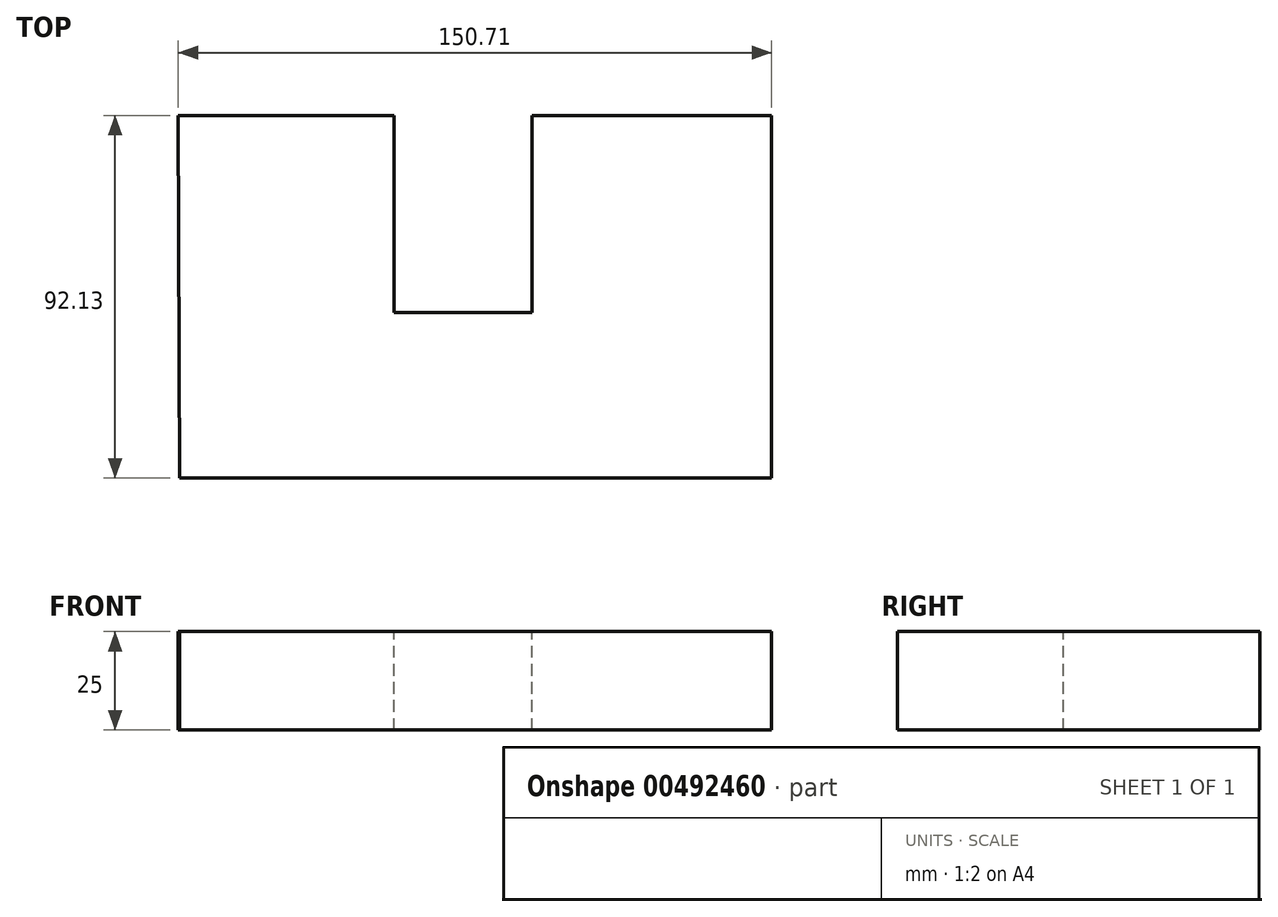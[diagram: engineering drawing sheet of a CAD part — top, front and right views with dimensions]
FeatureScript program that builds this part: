
annotation { "Feature Type Name" : "Feature", "Feature Type Description" : "" }
export const myFeature = defineFeature(function(context is Context, id is Id, definition is map)
    precondition{}
    {
        {
            var Q0;
            Q0=qCreatedBy(makeId("Top.planeOp"),FACE);
            var sketch = newSketch(context, id + "F0", { "sketchPlane" : qUnion([Q0])});
            skLineSegment(sketch, "E0", {"start": v(-75.26, 36.66) * mm, "end": v(75.45, 36.66) * mm});
            skLineSegment(sketch, "E1", {"start": v(75.45, 36.66) * mm, "end": v(75.45, -55.47) * mm});
            skLineSegment(sketch, "E2", {"start": v(-74.87, -55.47) * mm, "end": v(-75.26, 36.66) * mm});
            skLineSegment(sketch, "E3", {"start": v(-74.87, -55.47) * mm, "end": v(75.45, -55.47) * mm});
            skSolve(sketch);
        }
        {
            var Q0;
            Q0=makeQuery(id+"F0.imprint","IMPRINT",FACE,{"disambiguationData":[TD([[makeQuery(id+"F0.imprint","IMPRINT",EDGE,{"derivedFrom":sQuery(id+"F0.wireOp",EDGE,"E0")}),-1.0]])]});
            extrude(context, id + "F1", {"entities" : qUnion([Q0]), "depth" : 25 * mm});
        }
        {
            var Q0;
            Q0=makeQuery(id+"F1.opExtrude","CAP_FACE",FACE,{"disambiguationData":[OSD([sQuery(id+"F0.wireOp",EDGE,"E0"),sQuery(id+"F0.wireOp",EDGE,"E1"),sQuery(id+"F0.wireOp",EDGE,"E2"),sQuery(id+"F0.wireOp",EDGE,"E3")])],"isStart":false});
            var sketch = newSketch(context, id + "F2", { "sketchPlane" : qUnion([Q0])});
            skLineSegment(sketch, "E4", {"start": v(-20.42, 36.66) * mm, "end": v(-20.42, -13.34) * mm});
            skLineSegment(sketch, "E5", {"start": v(14.6, 36.66) * mm, "end": v(14.6, -13.34) * mm});
            skLineSegment(sketch, "E6", {"start": v(-20.42, -13.34) * mm, "end": v(14.6, -13.34) * mm});
            skSolve(sketch);
        }
        {
            var Q0;
            {var subQ0=sQuery(id+"F2.wireOp",EDGE,"E4");Q0=makeQuery(id+"F2.imprint","IMPRINT",FACE,{"disambiguationData":[TD([[makeQuery(id+"F2.imprint","IMPRINT",EDGE,{"derivedFrom":subQ0}),1.0]])]});}
            extrude(context, id + "F3", {"entities" : qUnion([Q0]), "operationType" : NewBodyOperationType.REMOVE, "oppositeDirection" : true, "depth" : 40.3 * mm});
        }
        {
            var Q0;
            Q0=makeQuery(id+"F3.boolean.opBoolean","COPY",FACE,{"derivedFrom":makeQuery(id+"F3.opExtrude","SWEPT_FACE",FACE,{"disambiguationData":[OSD([sQuery(id+"F2.wireOp",EDGE,"E6")])]})});
            var sketch = newSketch(context, id + "F4", { "sketchPlane" : qUnion([Q0])});
            skLineSegment(sketch, "E7", {"start": v(20.42, 0) * mm, "end": v(-14.6, 0) * mm});
            skSolve(sketch);
        }
        {
            var Q0;
            Q0=sQuery(id+"F4.wireOp",EDGE,"E7");
            extrude(context, id + "F5", {"bodyType" : ToolBodyType.SURFACE, "surfaceEntities" : qUnion([Q0]), "depth" : 50 * mm});
        }
    });
